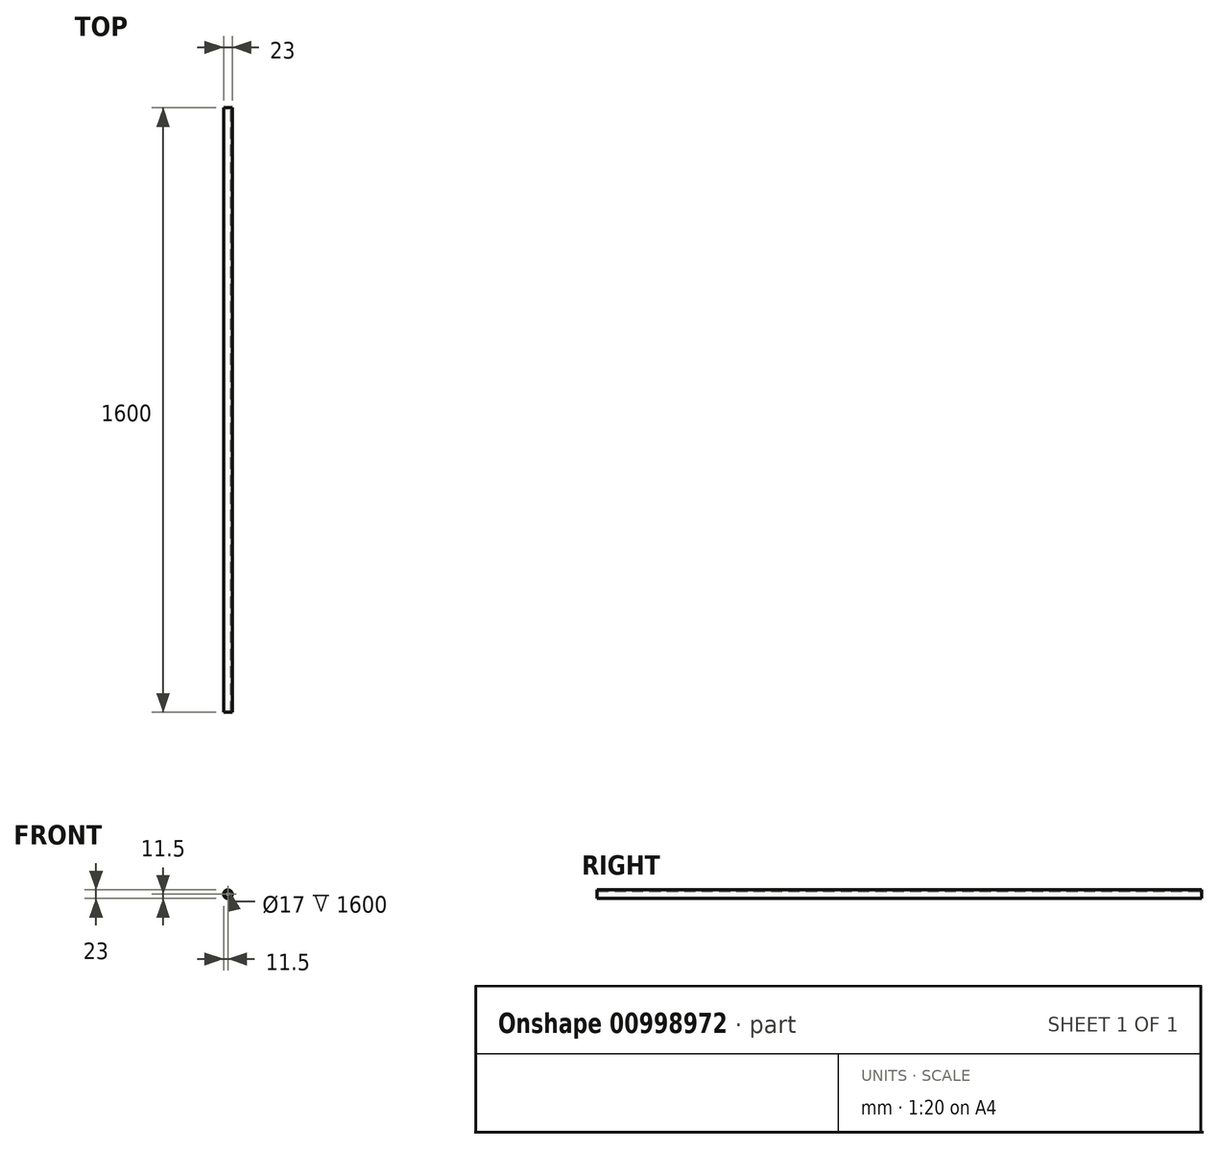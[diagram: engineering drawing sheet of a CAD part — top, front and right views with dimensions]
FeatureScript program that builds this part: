
annotation { "Feature Type Name" : "Feature", "Feature Type Description" : "" }
export const myFeature = defineFeature(function(context is Context, id is Id, definition is map)
    precondition{}
    {
        {
            var Q0;
            Q0=qCreatedBy(makeId("Front.planeOp"),FACE);
            var sketch = newSketch(context, id + "F0", { "sketchPlane" : qUnion([Q0])});
            skCircle(sketch, "E0", {"center": v(0, 0) * mm, "radius": 11.5 * mm});
            skCircle(sketch, "E1", {"center": v(0, 0) * mm, "radius": 8.5 * mm});
            skSolve(sketch);
        }
        {
            var Q0;
            Q0 = qSketchRegion(id + "F0", true);
            extrude(context, id + "F1", {"entities" : qUnion([Q0]), "depth" : 1600 * mm, "offsetDistance" : 25 * mm});
        }
    });
